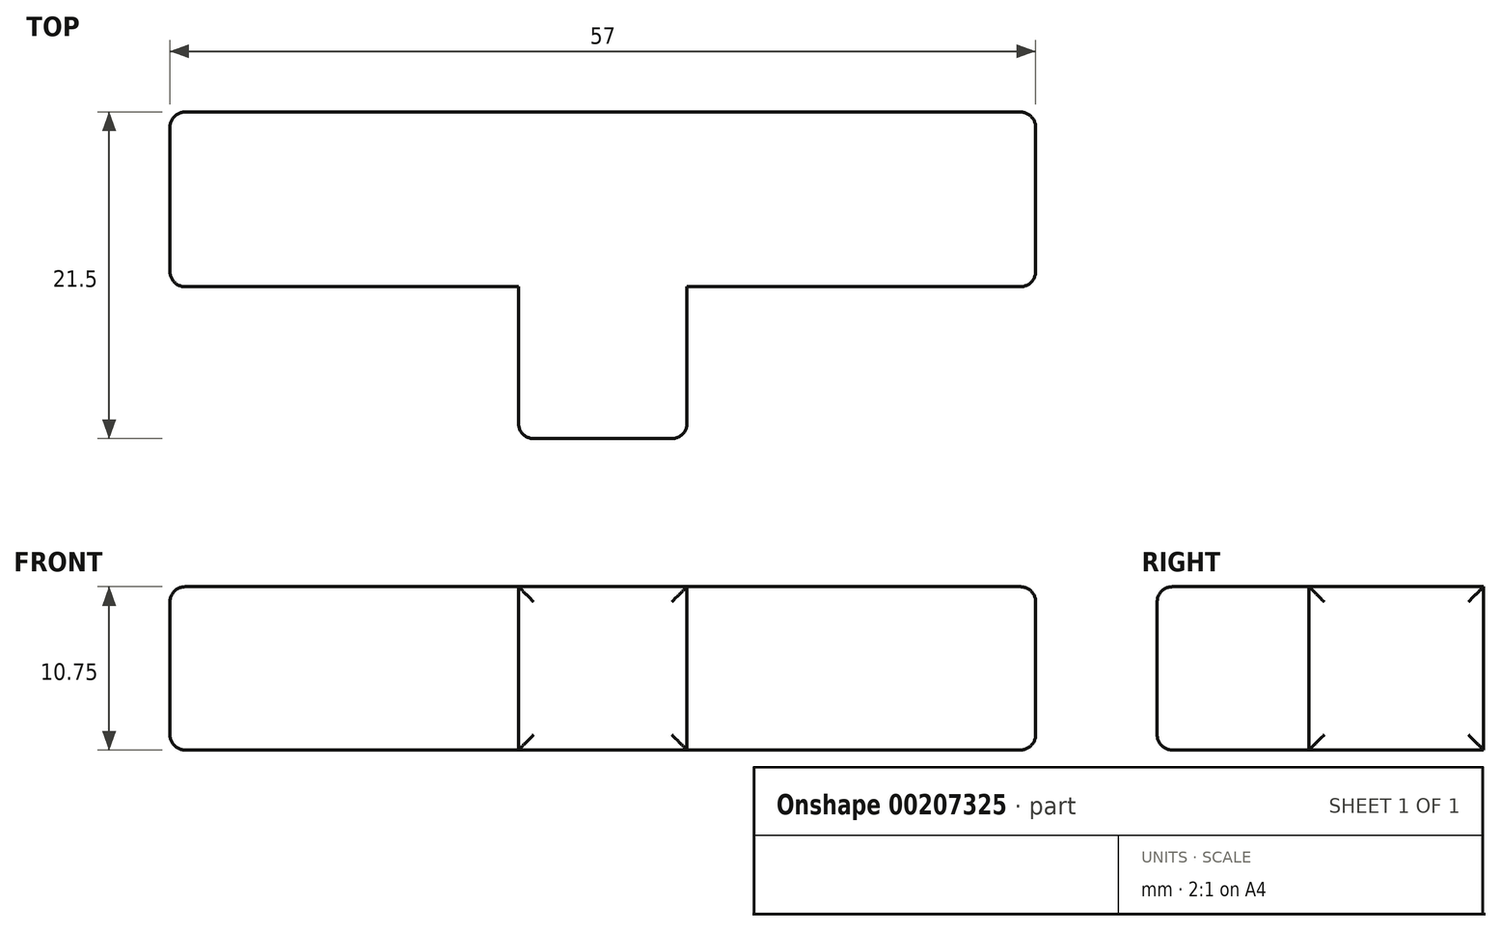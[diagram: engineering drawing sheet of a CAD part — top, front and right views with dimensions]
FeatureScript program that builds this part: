
annotation { "Feature Type Name" : "Feature", "Feature Type Description" : "" }
export const myFeature = defineFeature(function(context is Context, id is Id, definition is map)
    precondition{}
    {
        {
            var Q0;
            Q0=qCreatedBy(makeId("Front.planeOp"),FACE);
            var sketch = newSketch(context, id + "F0", { "sketchPlane" : qUnion([Q0])});
            skLineSegment(sketch, "E0.bottom", {"start": v(-28.5, 5.4) * mm, "end": v(28.5, 5.4) * mm});
            skLineSegment(sketch, "E0.top", {"start": v(-28.5, -5.34) * mm, "end": v(28.5, -5.34) * mm});
            skLineSegment(sketch, "E0.left", {"start": v(-28.5, 5.4) * mm, "end": v(-28.5, -5.34) * mm});
            skLineSegment(sketch, "E0.right", {"start": v(28.5, 5.4) * mm, "end": v(28.5, -5.34) * mm});
            skSolve(sketch);
        }
        {
            var Q0;
            Q0=makeQuery(id+"F0.imprint","IMPRINT",FACE,{"disambiguationData":[TD([[makeQuery(id+"F0.imprint","IMPRINT",EDGE,{"derivedFrom":sQuery(id+"F0.wireOp",EDGE,"E0.bottom")}),-1.0]])]});
            extrude(context, id + "F1", {"entities" : qUnion([Q0]), "depth" : 11.5 * mm});
        }
        {
            var Q0;
            Q0=makeQuery(id+"F1.opExtrude","CAP_FACE",FACE,{"disambiguationData":[OSD([sQuery(id+"F0.wireOp",EDGE,"E0.bottom"),sQuery(id+"F0.wireOp",EDGE,"E0.top"),sQuery(id+"F0.wireOp",EDGE,"E0.left"),sQuery(id+"F0.wireOp",EDGE,"E0.right")])],"isStart":false});
            var sketch = newSketch(context, id + "F2", { "sketchPlane" : qUnion([Q0])});
            skLineSegment(sketch, "E1.bottom", {"start": v(-5.55, 5.4) * mm, "end": v(5.55, 5.4) * mm});
            skLineSegment(sketch, "E1.top", {"start": v(-5.55, -5.4) * mm, "end": v(5.55, -5.4) * mm});
            skLineSegment(sketch, "E1.left", {"start": v(-5.55, 5.4) * mm, "end": v(-5.55, -5.4) * mm});
            skLineSegment(sketch, "E1.right", {"start": v(5.55, 5.4) * mm, "end": v(5.55, -5.4) * mm});
            skPoint(sketch, "E1.middle", {"position": v(0, 0) * mm});
            skSolve(sketch);
        }
        {
            var Q0;
            {var subQ0=sQuery(id+"F2.wireOp",EDGE,"E1.bottom");Q0=makeQuery(id+"F2.imprint","IMPRINT",FACE,{"disambiguationData":[TD([[makeQuery(id+"F2.imprint","IMPRINT",EDGE,{"derivedFrom":subQ0}),-1.0]])]});}
            extrude(context, id + "F3", {"entities" : qUnion([Q0]), "operationType" : NewBodyOperationType.ADD, "depth" : 10 * mm});
        }
        {
            var Q0;
            Q0=makeQuery(id+"F3.opExtrude","CAP_EDGE",EDGE,{"disambiguationData":[OSD([sQuery(id+"F2.wireOp",EDGE,"E1.right")])],"isStart":false});
            var Q1;
            Q1=makeQuery(id+"F3.opExtrude","CAP_EDGE",EDGE,{"disambiguationData":[OSD([sQuery(id+"F2.wireOp",EDGE,"E1.bottom")])],"isStart":false});
            var Q2;
            Q2=makeQuery(id+"F3.opExtrude","CAP_EDGE",EDGE,{"disambiguationData":[OSD([sQuery(id+"F2.wireOp",EDGE,"E1.left")])],"isStart":false});
            var Q3;
            Q3=makeQuery(id+"F3.opExtrude","CAP_EDGE",EDGE,{"disambiguationData":[OSD([sQuery(id+"F0.wireOp",EDGE,"E0.top")])],"isStart":false});
            var Q4;
            Q4=makeQuery(id+"F1.opExtrude","CAP_EDGE",EDGE,{"disambiguationData":[OSD([sQuery(id+"F0.wireOp",EDGE,"E0.right")])],"isStart":false});
            var Q5;
            Q5=makeQuery(id+"F1.opExtrude","SWEPT_EDGE",EDGE,{"disambiguationData":[OSD([sQuery(id+"F0.wireOp",EDGE,"E0.bottom"),sQuery(id+"F0.wireOp",EDGE,"E0.right")])]});
            var Q6;
            Q6=makeQuery(id+"F1.opExtrude","SWEPT_EDGE",EDGE,{"disambiguationData":[OSD([sQuery(id+"F0.wireOp",EDGE,"E0.top"),sQuery(id+"F0.wireOp",EDGE,"E0.right")])]});
            var Q7;
            Q7=makeQuery(id+"F1.opExtrude","CAP_EDGE",EDGE,{"disambiguationData":[OSD([sQuery(id+"F0.wireOp",EDGE,"E0.right")])],"isStart":true});
            var Q8;
            Q8=makeQuery(id+"F1.opExtrude","SWEPT_EDGE",EDGE,{"disambiguationData":[OSD([sQuery(id+"F0.wireOp",EDGE,"E0.bottom"),sQuery(id+"F0.wireOp",EDGE,"E0.left")])]});
            var Q9;
            Q9=makeQuery(id+"F1.opExtrude","CAP_EDGE",EDGE,{"disambiguationData":[OSD([sQuery(id+"F0.wireOp",EDGE,"E0.left")])],"isStart":false});
            var Q10;
            Q10=makeQuery(id+"F1.opExtrude","SWEPT_EDGE",EDGE,{"disambiguationData":[OSD([sQuery(id+"F0.wireOp",EDGE,"E0.top"),sQuery(id+"F0.wireOp",EDGE,"E0.left")])]});
            var Q11;
            Q11=makeQuery(id+"F1.opExtrude","CAP_EDGE",EDGE,{"disambiguationData":[OSD([sQuery(id+"F0.wireOp",EDGE,"E0.left")])],"isStart":true});
            fillet(context, id + "F4", {"entities" : qUnion([Q0, Q1, Q2, Q3, Q4, Q5, Q6, Q7, Q8, Q9, Q10, Q11]), "radius" : 1 * mm, "tangentPropagation" : true, "allowEdgeOverflow" : false});
        }
    });
